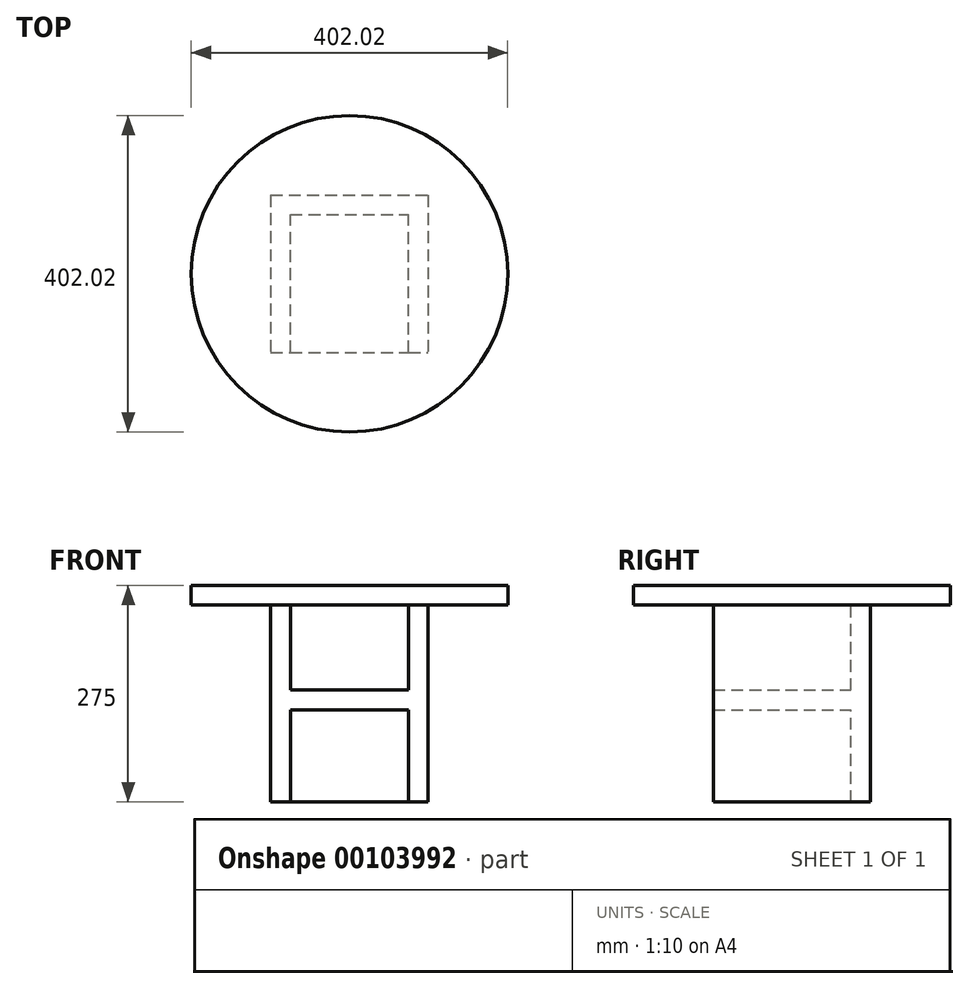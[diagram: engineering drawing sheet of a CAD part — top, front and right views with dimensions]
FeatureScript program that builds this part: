
annotation { "Feature Type Name" : "Feature", "Feature Type Description" : "" }
export const myFeature = defineFeature(function(context is Context, id is Id, definition is map)
    precondition{}
    {
        {
            var Q0;
            Q0=qCreatedBy(makeId("Top.planeOp"),FACE);
            var sketch = newSketch(context, id + "F0", { "sketchPlane" : qUnion([Q0])});
            skLineSegment(sketch, "E0.bottom", {"start": v(-100, 100) * mm, "end": v(100, 100) * mm});
            skLineSegment(sketch, "E0.top", {"start": v(-100, -100) * mm, "end": v(100, -100) * mm});
            skLineSegment(sketch, "E0.left", {"start": v(-100, 100) * mm, "end": v(-100, -100) * mm});
            skLineSegment(sketch, "E0.right", {"start": v(100, 100) * mm, "end": v(100, -100) * mm});
            skPoint(sketch, "E0.middle", {"position": v(0, 0) * mm});
            skSolve(sketch);
        }
        {
            var Q0;
            Q0=makeQuery(id+"F0.imprint","IMPRINT",FACE,{"disambiguationData":[TD([[makeQuery(id+"F0.imprint","IMPRINT",EDGE,{"derivedFrom":sQuery(id+"F0.wireOp",EDGE,"E0.bottom")}),-1.0]])]});
            extrude(context, id + "F1", {"entities" : qUnion([Q0]), "oppositeDirection" : true, "depth" : 250 * mm});
        }
        {
            var Q0;
            Q0=makeQuery(id+"F1.opExtrude","SWEPT_FACE",FACE,{"disambiguationData":[OSD([sQuery(id+"F0.wireOp",EDGE,"E0.top")])]});
            var Q1;
            Q1=makeQuery(id+"F1.opExtrude","CAP_FACE",FACE,{"disambiguationData":[OSD([sQuery(id+"F0.wireOp",EDGE,"E0.bottom"),sQuery(id+"F0.wireOp",EDGE,"E0.top"),sQuery(id+"F0.wireOp",EDGE,"E0.left"),sQuery(id+"F0.wireOp",EDGE,"E0.right")])],"isStart":true});
            var Q2;
            Q2=makeQuery(id+"F1.opExtrude","CAP_FACE",FACE,{"disambiguationData":[OSD([sQuery(id+"F0.wireOp",EDGE,"E0.bottom"),sQuery(id+"F0.wireOp",EDGE,"E0.top"),sQuery(id+"F0.wireOp",EDGE,"E0.left"),sQuery(id+"F0.wireOp",EDGE,"E0.right")])],"isStart":false});
            shell(context, id + "F2", {"entities" : qUnion([Q0, Q1, Q2]), "thickness" : 25 * mm});
        }
        {
            var Q0;
            Q0=makeQuery(id+"F2.opShell","OFFSET_FACE",FACE,{"disambiguationData":[OSD([sQuery(id+"F0.wireOp",EDGE,"E0.bottom")])]});
            var sketch = newSketch(context, id + "F3", { "sketchPlane" : qUnion([Q0])});
            skLineSegment(sketch, "E1.bottom", {"start": v(-87.07, -107.86) * mm, "end": v(88, -107.86) * mm});
            skLineSegment(sketch, "E1.top", {"start": v(-87.07, -133.14) * mm, "end": v(88, -133.14) * mm});
            skLineSegment(sketch, "E1.left", {"start": v(-87.07, -107.86) * mm, "end": v(-87.07, -133.14) * mm});
            skLineSegment(sketch, "E1.right", {"start": v(88, -107.86) * mm, "end": v(88, -133.14) * mm});
            skSolve(sketch);
        }
        {
            var Q0;
            {var subQ0=sQuery(id+"F3.wireOp",EDGE,"E1.bottom");var subQ1=sQuery(id+"F0.wireOp",EDGE,"E0.bottom");var subQ2=makeQuery(id+"F2.opShell","OFFSET_EDGE",EDGE,{"disambiguationData":[OSD([subQ1,sQuery(id+"F0.wireOp",EDGE,"E0.left")])]});var subQ3=makeQuery(id+"F3.imprint","INTERSECT",VERTEX,{"derivedFrom":[subQ2,subQ0]});Q0=makeQuery(id+"F3.imprint","IMPRINT",FACE,{"disambiguationData":[TD([[makeQuery(id+"F3.imprint","IMPRINT",EDGE,{"disambiguationData":[TD([[subQ3,-1.0]])],"derivedFrom":subQ0}),-1.0]])]});}
            extrude(context, id + "F4", {"entities" : qUnion([Q0]), "operationType" : NewBodyOperationType.ADD, "depth" : 175 * mm});
        }
        {
            var Q0;
            Q0=makeQuery(id+"F1.opExtrude","CAP_FACE",FACE,{"disambiguationData":[OSD([sQuery(id+"F0.wireOp",EDGE,"E0.bottom"),sQuery(id+"F0.wireOp",EDGE,"E0.top"),sQuery(id+"F0.wireOp",EDGE,"E0.left"),sQuery(id+"F0.wireOp",EDGE,"E0.right")])],"isStart":true});
            var sketch = newSketch(context, id + "F5", { "sketchPlane" : qUnion([Q0])});
            skCircle(sketch, "E2", {"center": v(0, 0) * mm, "radius": 201.01 * mm});
            skSolve(sketch);
        }
        {
            var Q0;
            Q0=makeQuery(id+"F5.imprint","IMPRINT",FACE,{"disambiguationData":[TD([[makeQuery(id+"F5.imprint","IMPRINT",EDGE,{"derivedFrom":sQuery(id+"F5.wireOp",EDGE,"E2")}),1.0]])]});
            var Q1;
            {var subQ0=sQuery(id+"F0.wireOp",EDGE,"E0.bottom");var subQ1=makeQuery(id+"F1.opExtrude","CAP_EDGE",EDGE,{"disambiguationData":[OSD([subQ0])],"isStart":true});Q1=makeQuery(id+"F5.imprint","IMPRINT",FACE,{"disambiguationData":[TD([[makeQuery(id+"F5.imprint","IMPRINT",EDGE,{"derivedFrom":subQ1}),-1.0]])]});}
            extrude(context, id + "F6", {"entities" : qUnion([Q0, Q1]), "operationType" : NewBodyOperationType.ADD, "depth" : 25 * mm});
        }
    });
